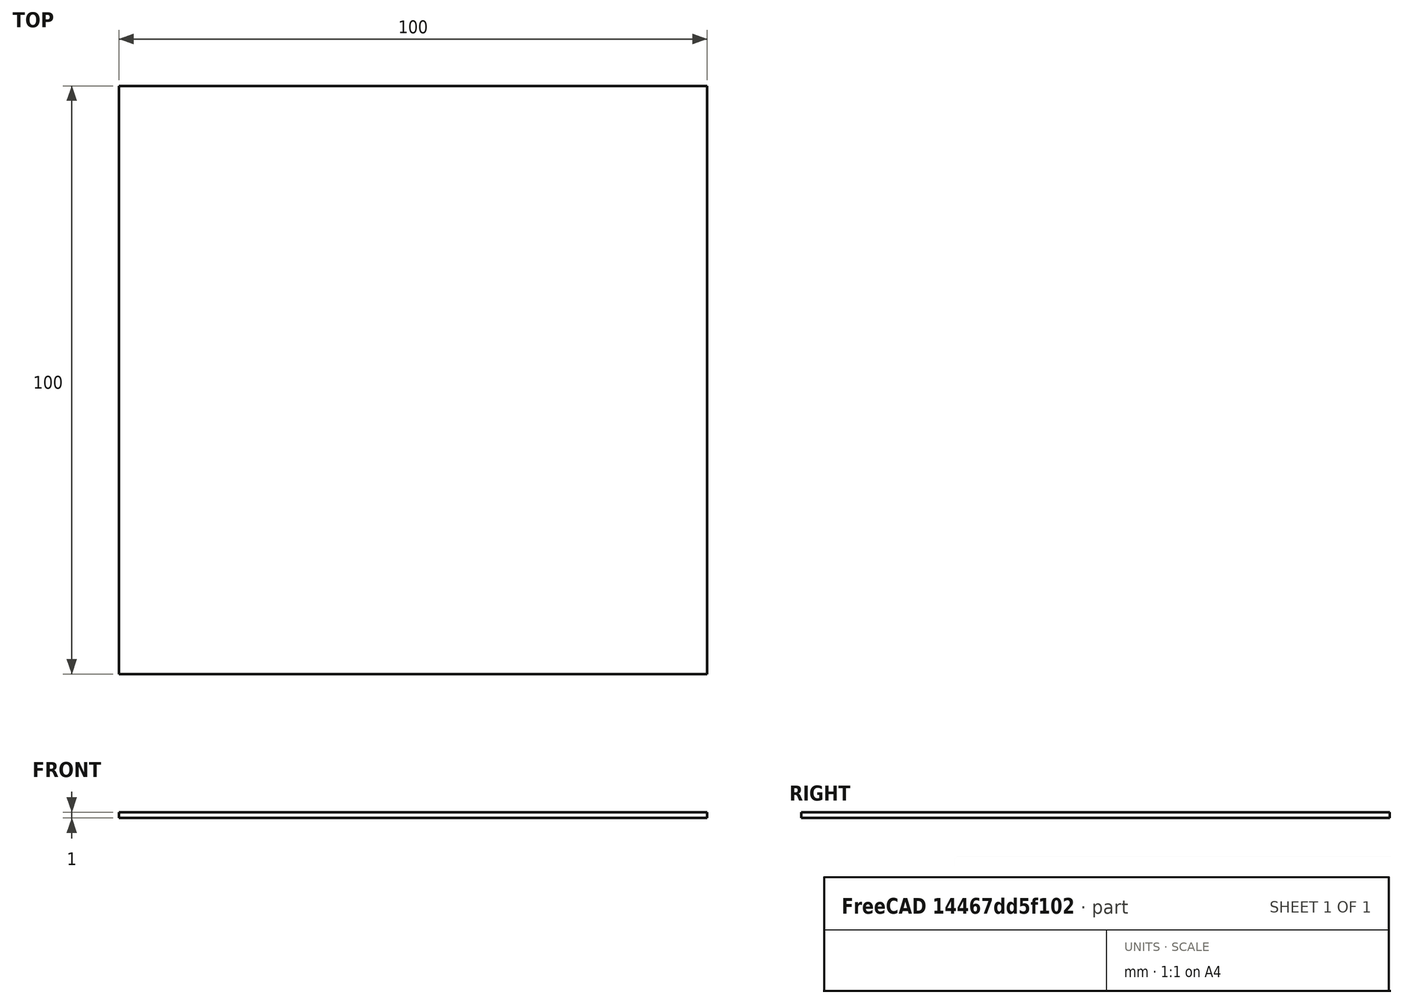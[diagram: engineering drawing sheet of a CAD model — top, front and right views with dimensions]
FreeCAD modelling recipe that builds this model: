
FCSTD DOCUMENT  (FreeCAD 1.0R39109 (Git))
Label: CalibrationPad
License: All rights reserved
LicenseURL: http://en.wikipedia.org/wiki/All_rights_reserved
objects: Sketcher::SketchObject×1, PartDesign::Pad×1, PartDesign::Body×1
note: 6 computed .brp shape members not serialized (recipe doc carries the construction recipe); baked Part::Feature solids carry a one-line shape summary decoded from their .brp

FEATURE [Sketcher::SketchObject] Sketch
  ArcFitTolerance = 1e-06
  AttachmentSupport = -> [XY_Plane]
  FullyConstrained = false
  MakeInternals = false
  MapMode = 5
  sketch-geometry (4):
    g0: LineSegment StartX=-30.2254 StartY=28.2787 StartZ=0 EndX=-30.2254 EndY=-71.7213 EndZ=0
    g1: LineSegment StartX=-30.2254 StartY=-71.7213 StartZ=0 EndX=69.7746 EndY=-71.7213 EndZ=0
    g2: LineSegment StartX=69.7746 StartY=-71.7213 StartZ=0 EndX=69.7746 EndY=28.2787 EndZ=0
    g3: LineSegment StartX=69.7746 StartY=28.2787 StartZ=0 EndX=-30.2254 EndY=28.2787 EndZ=0
  constraints (10):
    c: Coincident(g0,g1)
    c: Coincident(g1,g2)
    c: Coincident(g2,g3)
    c: Coincident(g3,g0)
    c: Vertical(g0)
    c: Vertical(g2)
    c: Horizontal(g1)
    c: Horizontal(g3)
    c: Distance(g0,g2) = 100
    c: Distance(g1,g3) = 100
FEATURE [PartDesign::Pad] Pad
  Direction = (0,0,1)
  Length = 1
  Length2 = 10
  Profile = -> Sketch
  ReferenceAxis = -> Sketch [N_Axis]
  Suppressed = false
  Type = 0
FEATURE [PartDesign::Body] Body
  AllowCompound = false
  Group = -> [Sketch,Pad]
  Origin = -> Origin
  Tip = -> Pad
